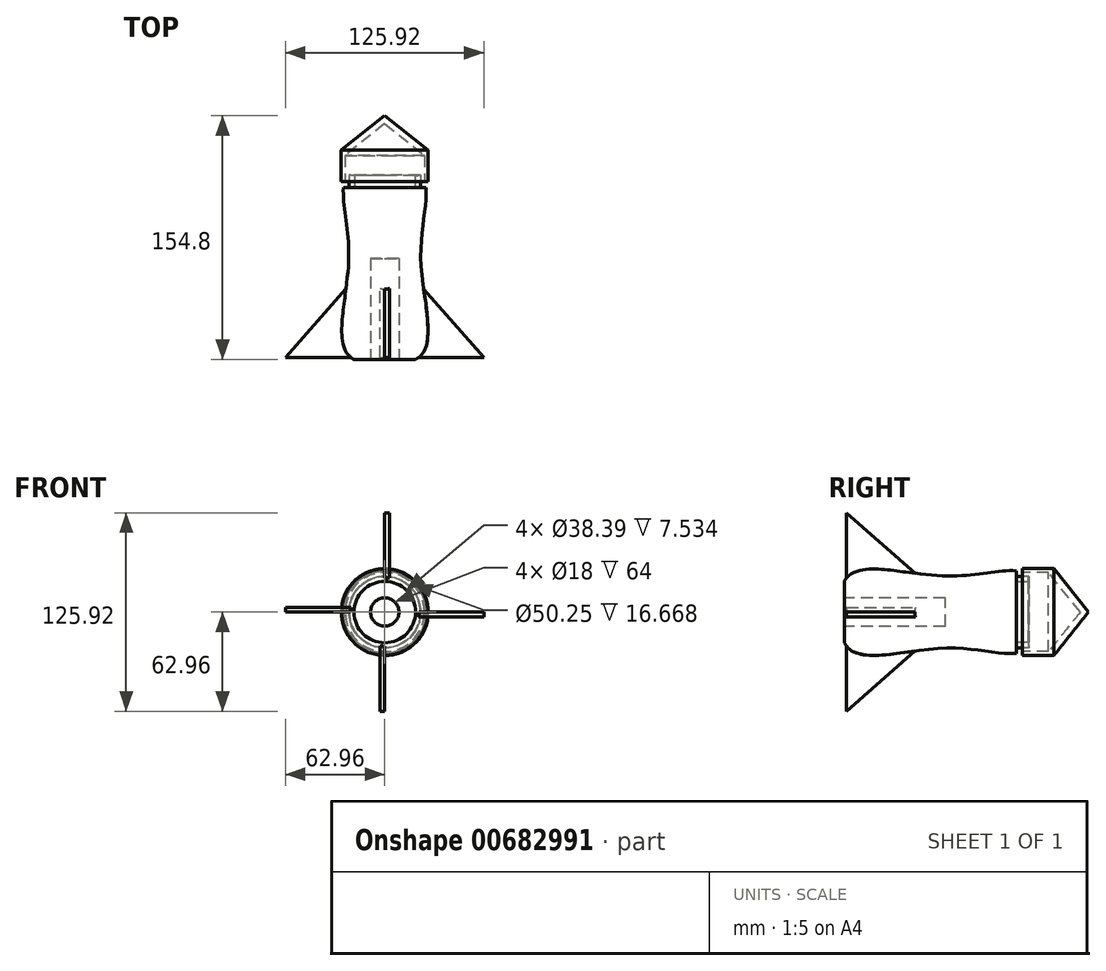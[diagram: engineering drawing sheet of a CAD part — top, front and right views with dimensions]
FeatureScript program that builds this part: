
annotation { "Feature Type Name" : "Feature", "Feature Type Description" : "" }
export const myFeature = defineFeature(function(context is Context, id is Id, definition is map)
    precondition{}
    {
        {
            var Q0;
            Q0=qCreatedBy(makeId("Top.planeOp"),FACE);
            var sketch = newSketch(context, id + "F0", { "sketchPlane" : qUnion([Q0])});
            skLineSegment(sketch, "E0", {"start": v(0, -77.41) * mm, "end": v(0, 78.33) * mm});
            skLineSegment(sketch, "E1", {"start": v(0, -76.47) * mm, "end": v(19.5, -76.47) * mm});
            skFitSpline(sketch, "E2", {"points": [v(19.5, -76.47) * mm, v(23.08, -16.94) * mm, v(26.23, 32.84) * mm], "startDerivative": vector(83.74, 38.64) * mm, "endDerivative": vector(-5.45, 85.75) * mm});
            skLineSegment(sketch, "E3", {"start": v(26.23, 32.84) * mm, "end": v(22.63, 32.84) * mm});
            skLineSegment(sketch, "E4", {"start": v(22.63, 32.84) * mm, "end": v(22.63, 40.56) * mm});
            skLineSegment(sketch, "E5", {"start": v(19.2, 40.37) * mm, "end": v(19.2, 32.84) * mm});
            skLineSegment(sketch, "E6", {"start": v(19.2, 32.84) * mm, "end": v(0, 32.84) * mm});
            skLineSegment(sketch, "E7", {"start": v(19.2, 40.37) * mm, "end": v(22.63, 40.56) * mm});
            skLineSegment(sketch, "E8", {"start": v(0, 78.33) * mm, "end": v(27.62, 56.53) * mm});
            skLineSegment(sketch, "E9", {"start": v(27.62, 56.53) * mm, "end": v(27.62, 36.5) * mm});
            skLineSegment(sketch, "E10", {"start": v(27.62, 36.5) * mm, "end": v(25.12, 36.5) * mm});
            skLineSegment(sketch, "E11", {"start": v(25.12, 36.5) * mm, "end": v(25.12, 53.17) * mm});
            skLineSegment(sketch, "E12", {"start": v(25.12, 53.17) * mm, "end": v(0, 73.33) * mm});
            skSolve(sketch);
        }
        {
            var Q0;
            {var subQ0=sQuery(id+"F0.wireOp",EDGE,"E8");Q0=makeQuery(id+"F0.imprint","IMPRINT",FACE,{"disambiguationData":[TD([[makeQuery(id+"F0.imprint","IMPRINT",EDGE,{"derivedFrom":subQ0}),-1.0]])]});}
            var Q1;
            {var subQ3=sQuery(id+"F0.wireOp",EDGE,"E1");Q1=makeQuery(id+"F0.imprint","IMPRINT",FACE,{"disambiguationData":[TD([[makeQuery(id+"F0.imprint","IMPRINT",EDGE,{"derivedFrom":subQ3}),1.0]])]});}
            var Q2;
            Q2=sQuery(id+"F0.wireOp",EDGE,"E0");
            revolve(context, id + "F1", {"entities" : qUnion([Q0, Q1]), "axis" : qUnion([Q2]), "revolveType" : RevolveType.FULL});
        }
        {
            var Q0;
            Q0=qCreatedBy(makeId("Top.planeOp"),FACE);
            var sketch = newSketch(context, id + "F2", { "sketchPlane" : qUnion([Q0])});
            skLineSegment(sketch, "E13", {"start": v(-20, -75.14) * mm, "end": v(-62.96, -75.14) * mm});
            skLineSegment(sketch, "E14", {"start": v(-62.96, -75.14) * mm, "end": v(-19.43, -25.66) * mm});
            skLineSegment(sketch, "E15", {"start": v(-19.43, -25.66) * mm, "end": v(-20, -75.14) * mm});
            skSolve(sketch);
        }
        {
            var Q0;
            Q0=makeQuery(id+"F2.imprint","IMPRINT",FACE,{"disambiguationData":[TD([[makeQuery(id+"F2.imprint","IMPRINT",EDGE,{"derivedFrom":sQuery(id+"F2.wireOp",EDGE,"E13")}),-1.0]])]});
            extrude(context, id + "F3", {"entities" : qUnion([Q0]), "operationType" : NewBodyOperationType.ADD, "depth" : 3 * mm, "offsetDistance" : 25 * mm});
        }
        {
            var Q0;
            Q0=makeQuery(id+"F1.opRevolve","SWEPT_BODY",BODY,{"disambiguationData":[OSD([sQuery(id+"F0.wireOp",EDGE,"E0"),sQuery(id+"F0.wireOp",EDGE,"E1"),sQuery(id+"F0.wireOp",EDGE,"E2"),sQuery(id+"F0.wireOp",EDGE,"E3"),sQuery(id+"F0.wireOp",EDGE,"E4"),sQuery(id+"F0.wireOp",EDGE,"E5"),sQuery(id+"F0.wireOp",EDGE,"E6"),sQuery(id+"F0.wireOp",EDGE,"E7")])]});
            var Q1;
            Q1=makeQuery(id+"F1.opRevolve","SWEPT_FACE",FACE,{"disambiguationData":[OSD([sQuery(id+"F0.wireOp",EDGE,"E2")])]});
            circularPattern(context, id + "F4", {"operationType" : NewBodyOperationType.ADD, "entities" : qUnion([Q0]), "axis" : qUnion([Q1]), "angle" : 360 * degree, "instanceCount" : 4, "equalSpace" : true});
        }
        {
            var Q0;
            Q0=makeQuery(id+"F1.opRevolve","SWEPT_FACE",FACE,{"disambiguationData":[OSD([sQuery(id+"F0.wireOp",EDGE,"E1")])]});
            var sketch = newSketch(context, id + "F5", { "sketchPlane" : qUnion([Q0])});
            skCircle(sketch, "E16", {"center": v(0, 0) * mm, "radius": 9 * mm});
            skSolve(sketch);
        }
        {
            var Q0;
            Q0 = qSketchRegion(id + "F5", true);
            extrude(context, id + "F6", {"entities" : qUnion([Q0]), "operationType" : NewBodyOperationType.REMOVE, "oppositeDirection" : true, "depth" : 64 * mm, "offsetDistance" : 25 * mm});
        }
    });
